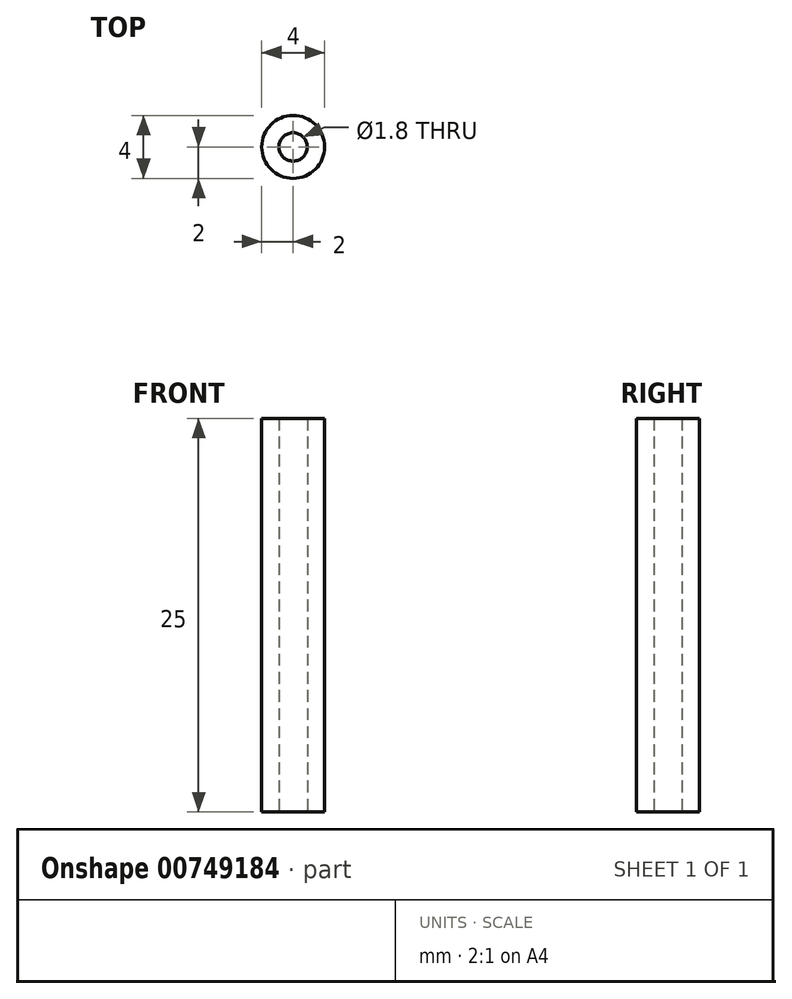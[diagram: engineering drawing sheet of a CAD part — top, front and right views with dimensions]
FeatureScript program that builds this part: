
annotation { "Feature Type Name" : "Feature", "Feature Type Description" : "" }
export const myFeature = defineFeature(function(context is Context, id is Id, definition is map)
    precondition{}
    {
        {
            var Q0;
            Q0=qCreatedBy(makeId("Top.planeOp"),FACE);
            var sketch = newSketch(context, id + "F0", { "sketchPlane" : qUnion([Q0])});
            skCircle(sketch, "E0", {"center": v(0, 0) * mm, "radius": 0.9 * mm});
            skCircle(sketch, "E1", {"center": v(0, 0) * mm, "radius": 2 * mm});
            skSolve(sketch);
        }
        {
            var Q0;
            Q0=qSketchRegion(id+"F0",true);
            extrude(context, id + "F1", {"entities" : qUnion([Q0]), "depth" : 25 * mm, "offsetDistance" : 25 * mm});
        }
    });
